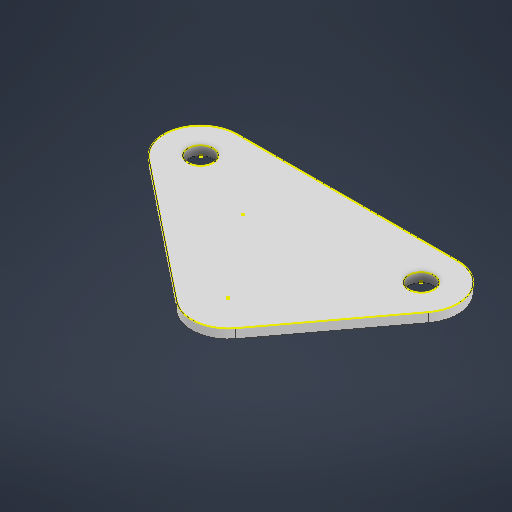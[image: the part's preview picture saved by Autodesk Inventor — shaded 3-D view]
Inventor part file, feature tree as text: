
AUTODESK INVENTOR PART (.ipt)
format: ipt  version: 2025 (Build 290162010, 162A)  size: 221,184 bytes
history: native  units: in
note: dims shown in document units (in); Inventor stores cm internally (conversion verified against a paired STEP export)
features: sketch x3, extrude x1
ambient origin geometry x8: Origin, YZ Plane, XZ Plane, XY Plane, X Axis, Y Axis, Z Axis, Center Point
bodies: Solid1 (feature_tree)
feature tree (4):
  extrude  "Extrusion1"  Depth=0.0625in
  sketch  "Sketch2"  dims[d10=0.172in]
  sketch  "Sketch3"  dims[d11=0.5in d16=1.5in d19=1.0in d20=0.5in]
  sketch  "Sketch1"  dims[d0=0.5in d3=0.0625in d4=0.0in d6=1.1022in]
